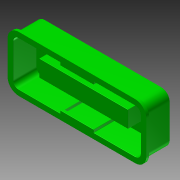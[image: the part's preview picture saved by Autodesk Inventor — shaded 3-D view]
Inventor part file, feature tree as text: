
AUTODESK INVENTOR PART (.ipt)
format: ipt  version: 2015 (Build 190159000, 159)  size: 242,176 bytes
history: native  units: in
note: dims shown in document units (in); Inventor stores cm internally (conversion verified against a paired STEP export)
features: fillet x7, extrude x5, sketch x5, mirror x4, plane x3, shell x2
ambient origin geometry x8: Origin, YZ Plane, XZ Plane, XY Plane, X Axis, Y Axis, Z Axis, Center Point
bodies: Solid1 (feature_tree)
feature tree (26):
  extrude  "Extrusion1"  Depth=0.5in
  fillet  "Fillet1"  Radius=0.47in
  shell  "Shell1"  Thickness=0.2in
  sketch  "Sketch2"  dims[d7=0.46in d8=0.2283in]
  plane  "Work Plane1"
  shell  "Shell2"  Thickness=0.1in
  extrude  "Extrusion5"  Depth=0.2283in
  plane  "Work Plane3"
  extrude  "Extrusion6"  Depth=0.47in TaperAngle=0.0deg
  plane  "Work Plane4"
  extrude  "Extrusion7"  Depth=0.01in
  fillet  "Fillet8"  Radius=0.05in
  mirror  "Mirror3"
  mirror  "Mirror4"
  fillet  "Fillet6"  Radius=0.05in
  fillet  "Fillet3"  Radius=0.445in
  fillet  "Fillet4"  Radius=0.05in
  extrude  "Extrusion2"  Depth=0.05in TaperAngle=0.0deg
  fillet  "Fillet2"  [1 undecoded]
  fillet  "Fillet7"  Radius=0.05in
  mirror  "Mirror1"
  mirror  "Mirror2"
  sketch  "Sketch1"  dims[d0=1.25in d1=0.5in d2=0.47in d3=0.0in d4=0.2in d5=0.1in]
  sketch  "Sketch4"  dims[d9=-0.033in d10=0.47in d11=0.0in]
  sketch  "Sketch5"  dims[d12=0.005in d13=0.01in d18=0.05in d23=0.05in d26=0.445in d28=0.05in]
  sketch  "Sketch6"  dims[d29=0.3in d30=0.05in d31=0.0in d32=-0.05in d33=0.05in d34=0.03in d35=0.4325in d36=0.0in d37=0.3in d38=0.8in d39=0.15in d40=0.005in d41=0.0in d42=0.005in]
note: 1 required parameter value undecoded (feature->parameter linkage not recoverable at this tier; creation-order binding heuristic only, values carry confidence <= 0.55)
